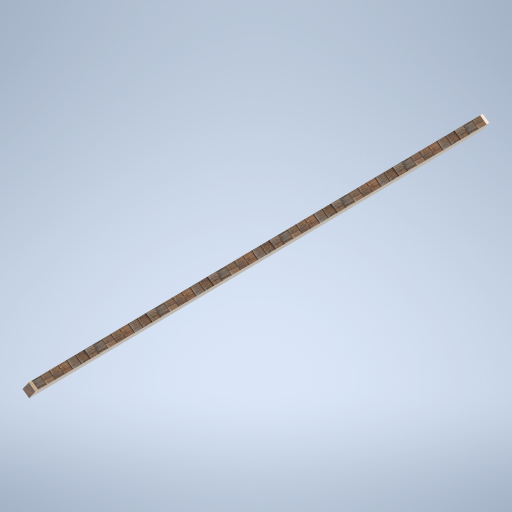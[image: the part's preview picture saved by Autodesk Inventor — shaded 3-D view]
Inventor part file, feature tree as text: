
AUTODESK INVENTOR PART (.ipt)
format: ipt  version: 2024.2 (Build 282272000, 272)  size: 304,128 bytes
history: native  units: in
note: dims shown in document units (in); Inventor stores cm internally (conversion verified against a paired STEP export)
features: sketch x5, other x3, plane x2
ambient origin geometry x8: Origin, YZ Plane, XZ Plane, XY Plane, X Axis, Y Axis, Z Axis, Center Point
bodies: Solid1 (feature_tree)
feature tree (10):
  other  "support_beam_segment_0106.ipt"
  other  "Solid1::support_beam_segment_0106.ipt"
  other  "TaggingFeature1"
  sketch  "Sketch1"  dims[d0=0.3937in]
  sketch  "Sketch2"
  sketch  "Sketch3"
  sketch  "Sketch4"
  sketch  "Sketch5"
  plane  "Work Plane1"
  plane  "Work Plane2"
